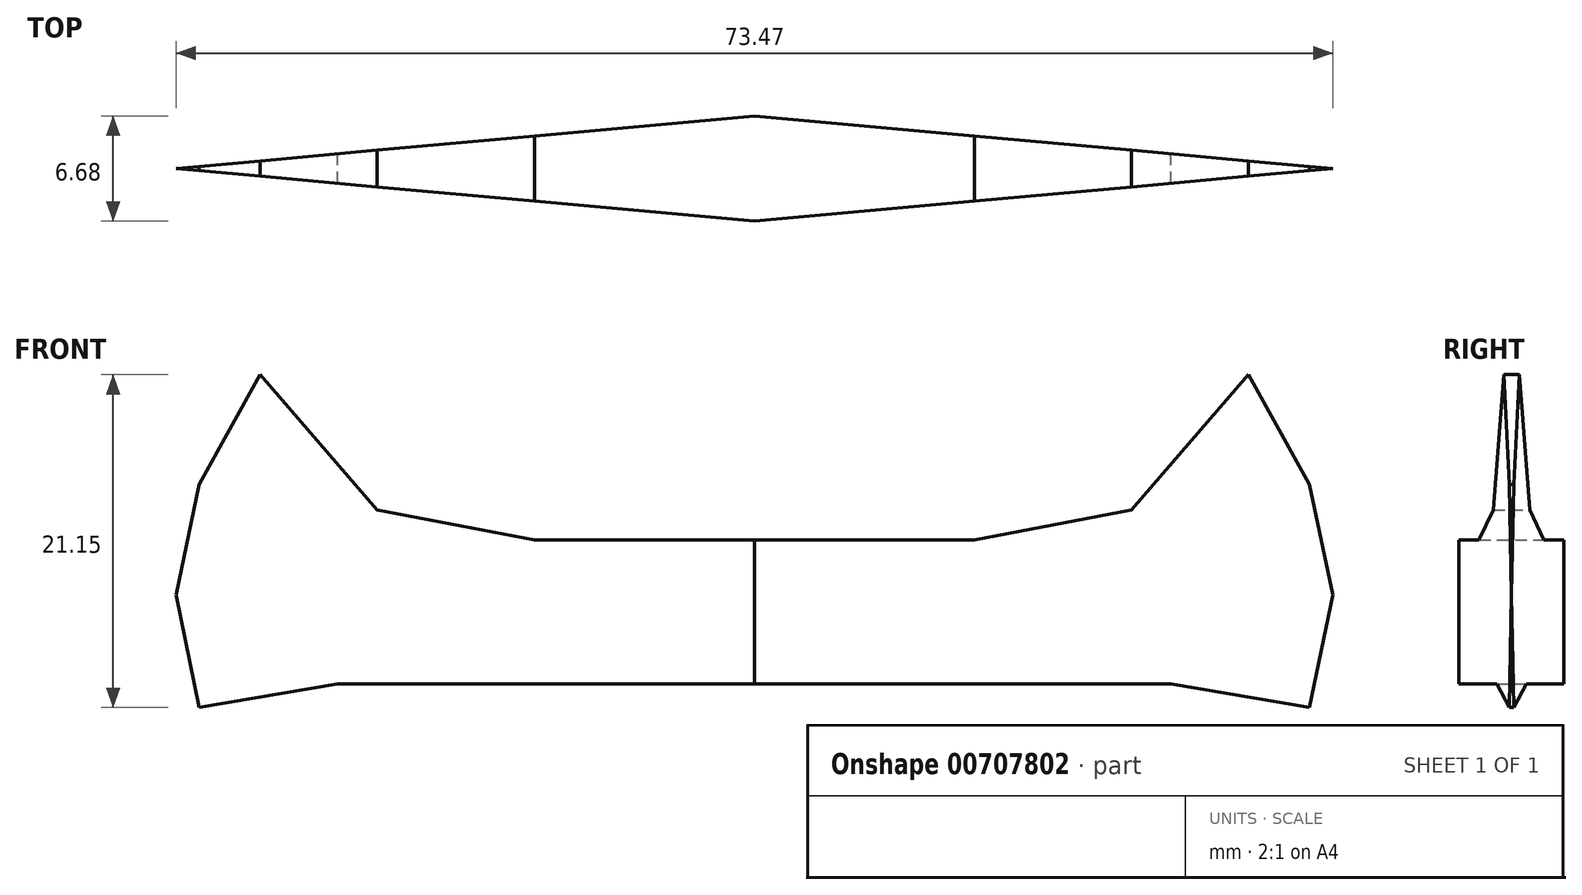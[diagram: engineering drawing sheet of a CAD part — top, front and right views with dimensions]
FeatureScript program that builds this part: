
annotation { "Feature Type Name" : "Feature", "Feature Type Description" : "" }
export const myFeature = defineFeature(function(context is Context, id is Id, definition is map)
    precondition{}
    {
        {
            var Q0;
            Q0=qCreatedBy(makeId("Front.planeOp"),FACE);
            var sketch = newSketch(context, id + "F0", { "sketchPlane" : qUnion([Q0])});
            skLineSegment(sketch, "E0", {"start": v(0, -26.91) * mm, "end": v(-13.98, -26.91) * mm});
            skLineSegment(sketch, "E1", {"start": v(-13.98, -26.91) * mm, "end": v(13.97, -26.91) * mm});
            skLineSegment(sketch, "E2", {"start": v(13.97, -26.91) * mm, "end": v(0, -26.91) * mm});
            skLineSegment(sketch, "E3", {"start": v(-13.98, -26.91) * mm, "end": v(-23.96, -25.02) * mm});
            skLineSegment(sketch, "E4", {"start": v(13.97, -26.91) * mm, "end": v(23.95, -25.02) * mm});
            skLineSegment(sketch, "E5", {"start": v(-31.39, -16.42) * mm, "end": v(-23.96, -25.02) * mm});
            skLineSegment(sketch, "E6", {"start": v(23.95, -25.02) * mm, "end": v(31.39, -16.42) * mm});
            skLineSegment(sketch, "E7", {"start": v(-31.39, -16.42) * mm, "end": v(-35.28, -23.41) * mm});
            skLineSegment(sketch, "E8", {"start": v(31.39, -16.42) * mm, "end": v(35.26, -23.41) * mm});
            skLineSegment(sketch, "E9", {"start": v(-36.73, -30.42) * mm, "end": v(-35.28, -23.41) * mm});
            skLineSegment(sketch, "E10", {"start": v(35.26, -23.41) * mm, "end": v(36.74, -30.42) * mm});
            skLineSegment(sketch, "E11", {"start": v(-35.28, -37.57) * mm, "end": v(-36.73, -30.42) * mm});
            skLineSegment(sketch, "E12", {"start": v(36.74, -30.42) * mm, "end": v(35.26, -37.57) * mm});
            skLineSegment(sketch, "E13", {"start": v(-26.48, -36.07) * mm, "end": v(-35.28, -37.57) * mm});
            skLineSegment(sketch, "E14", {"start": v(35.26, -37.57) * mm, "end": v(26.44, -36.07) * mm});
            skLineSegment(sketch, "E15", {"start": v(-26.48, -36.07) * mm, "end": v(26.44, -36.07) * mm});
            skSolve(sketch);
        }
        {
            var Q0;
            Q0=makeQuery(id+"F0.imprint","IMPRINT",FACE,{"disambiguationData":[TD([[makeQuery(id+"F0.imprint","IMPRINT",EDGE,{"derivedFrom":sQuery(id+"F0.wireOp",EDGE,"E1")}),-1.0]])]});
            extrude(context, id + "F1", {"entities" : qUnion([Q0]), "depth" : 6.35 * mm, "offsetDistance" : 25.4 * mm});
        }
        {
            var Q0;
            Q0=makeQuery(id+"F1.opExtrude","CAP_FACE",FACE,{"disambiguationData":[OSD([sQuery(id+"F0.wireOp",EDGE,"E1"),sQuery(id+"F0.wireOp",EDGE,"E2"),sQuery(id+"F0.wireOp",EDGE,"E3"),sQuery(id+"F0.wireOp",EDGE,"E4"),sQuery(id+"F0.wireOp",EDGE,"E5"),sQuery(id+"F0.wireOp",EDGE,"E6"),sQuery(id+"F0.wireOp",EDGE,"E7"),sQuery(id+"F0.wireOp",EDGE,"E8"),sQuery(id+"F0.wireOp",EDGE,"E9"),sQuery(id+"F0.wireOp",EDGE,"E10"),sQuery(id+"F0.wireOp",EDGE,"E11"),sQuery(id+"F0.wireOp",EDGE,"E12"),sQuery(id+"F0.wireOp",EDGE,"E13"),sQuery(id+"F0.wireOp",EDGE,"E14"),sQuery(id+"F0.wireOp",EDGE,"E15")])],"isStart":true});
            extrude(context, id + "F2", {"entities" : qUnion([Q0]), "operationType" : NewBodyOperationType.ADD, "depth" : 6.35 * mm, "offsetDistance" : 25.4 * mm});
        }
        {
            var Q0;
            Q0=qCreatedBy(makeId("Top.planeOp"),FACE);
            var sketch = newSketch(context, id + "F3", { "sketchPlane" : qUnion([Q0])});
            skLineSegment(sketch, "E16.bottom", {"start": v(25.81, -58.3) * mm, "end": v(-15.58, -58.3) * mm});
            skLineSegment(sketch, "E16.top", {"start": v(25.81, -39.13) * mm, "end": v(-15.58, -39.13) * mm});
            skLineSegment(sketch, "E16.left", {"start": v(25.81, -58.3) * mm, "end": v(25.81, -39.13) * mm});
            skLineSegment(sketch, "E16.right", {"start": v(-15.58, -58.3) * mm, "end": v(-15.58, -39.13) * mm});
            skSolve(sketch);
        }
        {
            var Q0;
            Q0=makeQuery(id+"F3.imprint","IMPRINT",FACE,{"disambiguationData":[TD([[makeQuery(id+"F3.imprint","IMPRINT",EDGE,{"derivedFrom":sQuery(id+"F3.wireOp",EDGE,"E16.bottom")}),-1.0]])]});
            extrude(context, id + "F4", {"entities" : qUnion([Q0]), "depth" : 25.4 * mm, "offsetDistance" : 25.4 * mm});
        }
        {
            var Q0;
            Q0=makeQuery(id+"F4.opExtrude","CAP_FACE",FACE,{"disambiguationData":[OSD([sQuery(id+"F3.wireOp",EDGE,"E16.bottom"),sQuery(id+"F3.wireOp",EDGE,"E16.top"),sQuery(id+"F3.wireOp",EDGE,"E16.left"),sQuery(id+"F3.wireOp",EDGE,"E16.right")])],"isStart":true});
            extrude(context, id + "F5", {"entities" : qUnion([Q0]), "operationType" : NewBodyOperationType.ADD, "depth" : 76.2 * mm, "offsetDistance" : 25.4 * mm});
        }
        {
            var Q0;
            Q0=makeQuery(id+"F5.opExtrude","CAP_FACE",FACE,{"disambiguationData":[OSD([sQuery(id+"F3.wireOp",EDGE,"E16.bottom"),sQuery(id+"F3.wireOp",EDGE,"E16.top"),sQuery(id+"F3.wireOp",EDGE,"E16.left"),sQuery(id+"F3.wireOp",EDGE,"E16.right")])],"isStart":false});
            var sketch = newSketch(context, id + "F6", { "sketchPlane" : qUnion([Q0])});
            skLineSegment(sketch, "E17", {"start": v(36.77, 0) * mm, "end": v(0, 3.34) * mm});
            skLineSegment(sketch, "E18", {"start": v(0, 3.34) * mm, "end": v(-36.77, 0) * mm});
            skLineSegment(sketch, "E19", {"start": v(-36.77, 0) * mm, "end": v(0, -3.34) * mm});
            skLineSegment(sketch, "E20", {"start": v(0, -3.34) * mm, "end": v(36.77, 0) * mm});
            skLineSegment(sketch, "E21.bottom", {"start": v(42.92, 9.18) * mm, "end": v(-44.6, 9.18) * mm});
            skLineSegment(sketch, "E21.top", {"start": v(42.92, -11.48) * mm, "end": v(-44.6, -11.48) * mm});
            skLineSegment(sketch, "E21.left", {"start": v(42.92, 9.18) * mm, "end": v(42.92, -11.48) * mm});
            skLineSegment(sketch, "E21.right", {"start": v(-44.6, 9.18) * mm, "end": v(-44.6, -11.48) * mm});
            skSolve(sketch);
        }
        {
            var Q0;
            Q0=makeQuery(id+"F6.imprint","IMPRINT",FACE,{"disambiguationData":[TD([[makeQuery(id+"F6.imprint","IMPRINT",EDGE,{"derivedFrom":sQuery(id+"F6.wireOp",EDGE,"E17")}),-1.0]])]});
            extrude(context, id + "F7", {"entities" : qUnion([Q0]), "operationType" : NewBodyOperationType.REMOVE, "oppositeDirection" : true, "depth" : 1270 * mm, "offsetDistance" : 25.4 * mm});
        }
        {
            var Q0;
            Q0=makeQuery(id+"F5.opExtrude","CAP_FACE",FACE,{"disambiguationData":[OSD([sQuery(id+"F3.wireOp",EDGE,"E16.bottom"),sQuery(id+"F3.wireOp",EDGE,"E16.top"),sQuery(id+"F3.wireOp",EDGE,"E16.left"),sQuery(id+"F3.wireOp",EDGE,"E16.right")])],"isStart":false});
            extrude(context, id + "F8", {"entities" : qUnion([Q0]), "operationType" : NewBodyOperationType.REMOVE, "oppositeDirection" : true, "depth" : 127 * mm, "offsetDistance" : 25.4 * mm});
        }
    });
